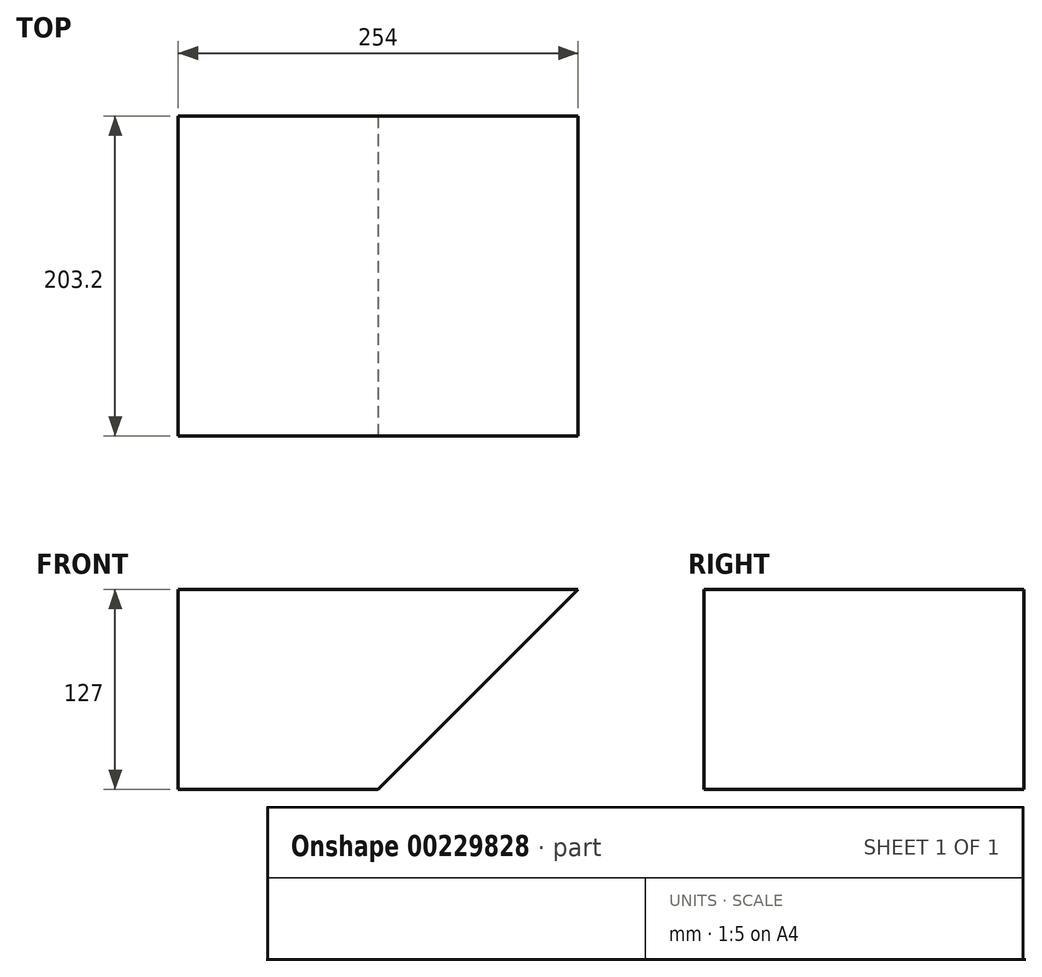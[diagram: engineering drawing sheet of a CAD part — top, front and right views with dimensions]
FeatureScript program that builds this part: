
annotation { "Feature Type Name" : "Feature", "Feature Type Description" : "" }
export const myFeature = defineFeature(function(context is Context, id is Id, definition is map)
    precondition{}
    {
        {
            var Q0;
            Q0=qCreatedBy(makeId("Front.planeOp"),FACE);
            var sketch = newSketch(context, id + "F0", { "sketchPlane" : qUnion([Q0])});
            skLineSegment(sketch, "E0.bottom", {"start": v(-254, 0) * mm, "end": v(0, 0) * mm});
            skLineSegment(sketch, "E0.top", {"start": v(-254, 127) * mm, "end": v(0, 127) * mm});
            skLineSegment(sketch, "E0.left", {"start": v(-254, 0) * mm, "end": v(-254, 127) * mm});
            skLineSegment(sketch, "E0.right", {"start": v(0, 0) * mm, "end": v(0, 127) * mm});
            skSolve(sketch);
        }
        {
            var Q0;
            Q0 = qSketchRegion(id + "F0", true);
            extrude(context, id + "F1", {"entities" : qUnion([Q0]), "depth" : 203.2 * mm});
        }
        {
            var Q0;
            Q0=makeQuery(id+"F1.opExtrude","SWEPT_EDGE",EDGE,{"disambiguationData":[OSD([sQuery(id+"F0.wireOp",EDGE,"E0.bottom"),sQuery(id+"F0.wireOp",EDGE,"E0.right")])]});
            chamfer(context, id + "F2", {"entities" : qUnion([Q0]), "chamferType" : ChamferType.OFFSET_ANGLE, "width" : 127 * mm, "oppositeDirection" : false, "angle" : 45 * degree, "tangentPropagation" : true});
        }
    });
